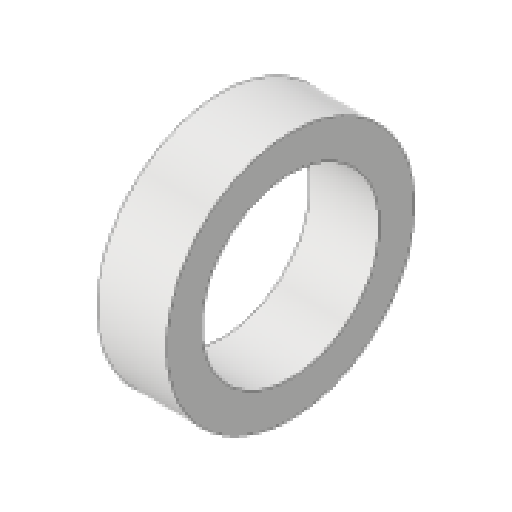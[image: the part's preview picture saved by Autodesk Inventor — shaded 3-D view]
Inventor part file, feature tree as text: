
AUTODESK INVENTOR PART (.ipt)
format: ipt  version: 2025.1 (Build 291241000, 241)  size: 105,472 bytes
history: native  units: mm
features: other x1, extrude x1, sketch x1
ambient origin geometry x8: Origin, YZ Plane, XZ Plane, XY Plane, X Axis, Y Axis, Z Axis, Center Point
bodies: Body1 (feature_tree)
feature tree (3):
  other  "Bryła1"
  extrude  "Wyciągnięcie proste1"  Depth=5.0mm
  sketch  "Szkic1"
